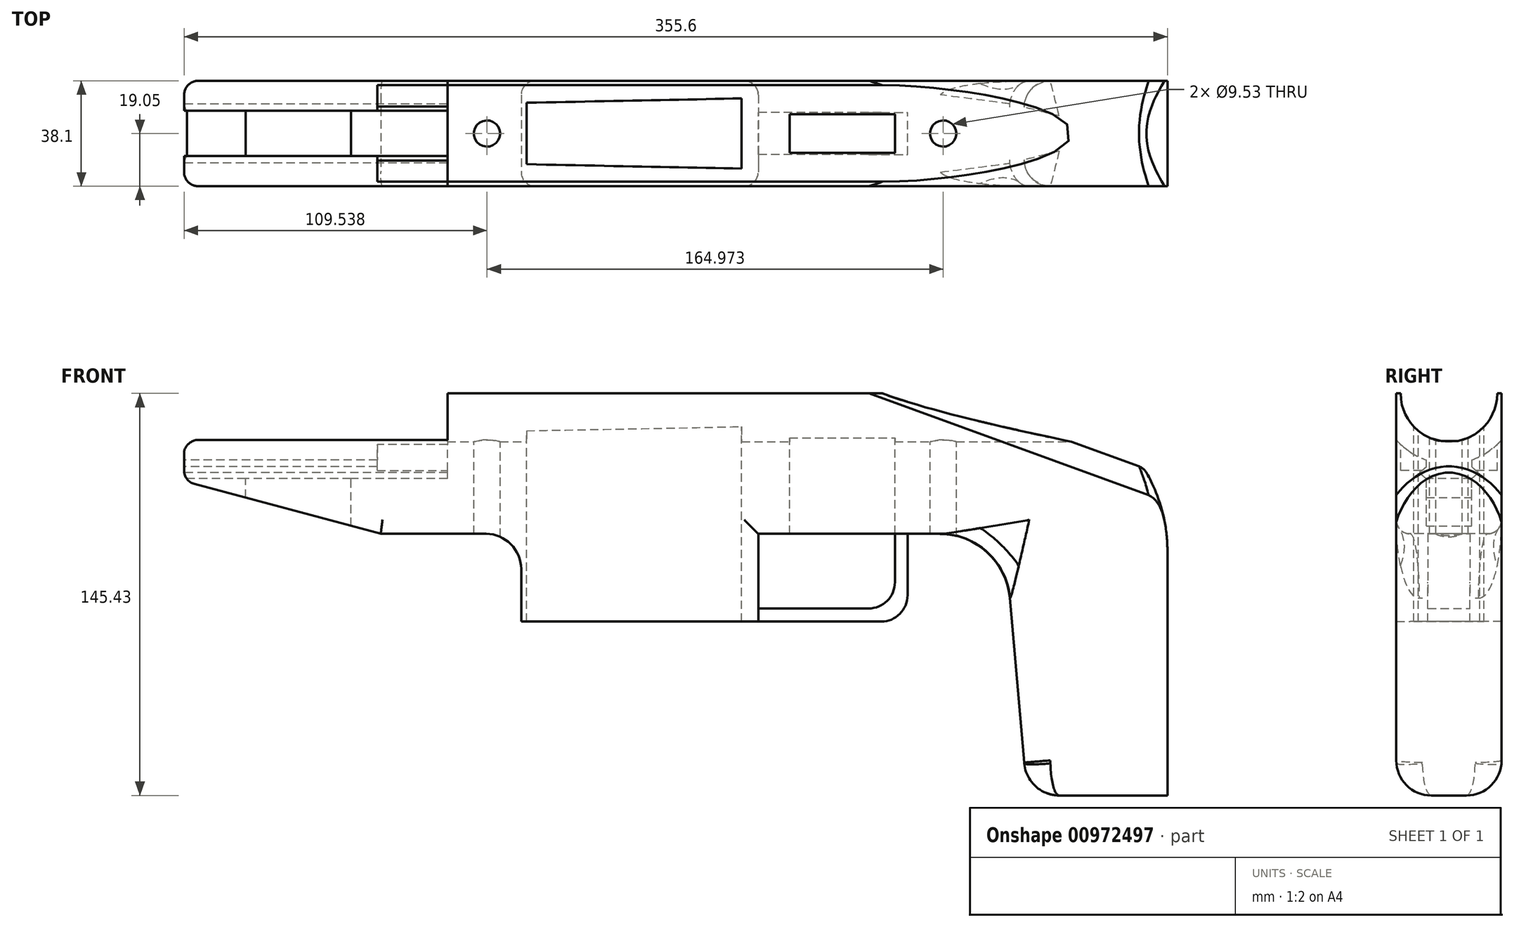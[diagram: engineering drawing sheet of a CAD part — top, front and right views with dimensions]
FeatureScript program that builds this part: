
annotation { "Feature Type Name" : "Feature", "Feature Type Description" : "" }
export const myFeature = defineFeature(function(context is Context, id is Id, definition is map)
    precondition{}
    {
        {
            var Q0;
            Q0=qCreatedBy(makeId("Front.planeOp"),FACE);
            var sketch = newSketch(context, id + "F0", { "sketchPlane" : qUnion([Q0])});
            skLineSegment(sketch, "E0", {"start": v(177.8, -57.15) * mm, "end": v(177.8, -145.43) * mm});
            skLineSegment(sketch, "E1", {"start": v(177.8, -145.43) * mm, "end": v(127, -145.43) * mm});
            skLineSegment(sketch, "E2", {"start": v(127, -145.43) * mm, "end": v(118.72, -50.8) * mm});
            skLineSegment(sketch, "E3", {"start": v(118.72, -50.8) * mm, "end": v(29.82, -50.8) * mm});
            skLineSegment(sketch, "E4", {"start": v(29.82, -50.8) * mm, "end": v(29.82, -82.55) * mm});
            skLineSegment(sketch, "E5", {"start": v(29.82, -82.55) * mm, "end": v(-55.9, -82.55) * mm});
            skLineSegment(sketch, "E6", {"start": v(-55.9, -82.55) * mm, "end": v(-55.9, -50.8) * mm});
            skLineSegment(sketch, "E7", {"start": v(-55.9, -50.8) * mm, "end": v(-106.7, -50.8) * mm});
            skLineSegment(sketch, "E8", {"start": v(-106.7, -50.8) * mm, "end": v(-177.8, -31.75) * mm});
            skLineSegment(sketch, "E9", {"start": v(-177.8, -31.75) * mm, "end": v(-177.8, -9.53) * mm});
            skLineSegment(sketch, "E10", {"start": v(-107.95, -9.53) * mm, "end": v(-107.95, 0) * mm});
            skLineSegment(sketch, "E11", {"start": v(-107.95, 0) * mm, "end": v(120.65, 0) * mm});
            skLineSegment(sketch, "E12", {"start": v(-107.95, -9.53) * mm, "end": v(-177.8, -9.53) * mm});
            skArc(sketch, "E13", {"start": v(177.8, -57.15) * mm, "mid": v(161.06, -16.74) * mm, "end": v(120.65, 0) * mm});
            skLineSegment(sketch, "E14", {"start": v(0, 57.34) * mm, "end": v(0, -146.77) * mm, "construction": true});
            skSolve(sketch);
        }
        {
            var Q0;
            Q0=makeQuery(id+"F0.imprint","IMPRINT",FACE,{"disambiguationData":[TD([[makeQuery(id+"F0.imprint","IMPRINT",EDGE,{"derivedFrom":sQuery(id+"F0.wireOp",EDGE,"E0")}),-1.0]])]});
            extrude(context, id + "F1", {"entities" : qUnion([Q0]), "oppositeDirection" : true, "depth" : 19.05 * mm, "offsetDistance" : 25.4 * mm, "hasSecondDirection" : true, "secondDirectionOppositeDirection" : false, "secondDirectionDepth" : 19.05 * mm});
        }
        {
            var Q0;
            Q0=makeQuery(id+"F1.opExtrude","CAP_EDGE",EDGE,{"disambiguationData":[OSD([sQuery(id+"F0.wireOp",EDGE,"E2")])],"isStart":true});
            var Q1;
            Q1=makeQuery(id+"F1.opExtrude","CAP_EDGE",EDGE,{"disambiguationData":[OSD([sQuery(id+"F0.wireOp",EDGE,"E2")])],"isStart":false});
            fillet(context, id + "F2", {"entities" : qUnion([Q0, Q1]), "radius" : 9.52 * mm, "tangentPropagation" : true, "allowEdgeOverflow" : false});
        }
        {
            var Q0;
            Q0=makeQuery(id+"F1.opExtrude","CAP_EDGE",EDGE,{"disambiguationData":[OSD([sQuery(id+"F0.wireOp",EDGE,"E1")])],"isStart":false});
            fillet(context, id + "F3", {"entities" : qUnion([Q0]), "radius" : 12.7 * mm, "tangentPropagation" : true, "allowEdgeOverflow" : false});
        }
        {
            var Q0;
            Q0=makeQuery(id+"F1.opExtrude","SWEPT_EDGE",EDGE,{"disambiguationData":[OSD([sQuery(id+"F0.wireOp",EDGE,"E6"),sQuery(id+"F0.wireOp",EDGE,"E7")])]});
            fillet(context, id + "F4", {"entities" : qUnion([Q0]), "radius" : 12.7 * mm, "tangentPropagation" : true, "allowEdgeOverflow" : false});
        }
        {
            var Q0;
            Q0=makeQuery(id+"F1.opExtrude","CAP_EDGE",EDGE,{"disambiguationData":[OSD([sQuery(id+"F0.wireOp",EDGE,"E3")])],"isStart":true});
            var Q1;
            Q1=makeQuery(id+"F1.opExtrude","CAP_EDGE",EDGE,{"disambiguationData":[OSD([sQuery(id+"F0.wireOp",EDGE,"E4")])],"isStart":true});
            var Q2;
            Q2=makeQuery(id+"F1.opExtrude","CAP_EDGE",EDGE,{"disambiguationData":[OSD([sQuery(id+"F0.wireOp",EDGE,"E6")])],"isStart":true});
            var Q3;
            Q3=makeQuery(id+"F1.opExtrude","CAP_EDGE",EDGE,{"disambiguationData":[OSD([sQuery(id+"F0.wireOp",EDGE,"E8")])],"isStart":true});
            var Q4;
            Q4=makeQuery(id+"F1.opExtrude","CAP_EDGE",EDGE,{"disambiguationData":[OSD([sQuery(id+"F0.wireOp",EDGE,"E3")])],"isStart":false});
            var Q5;
            Q5=makeQuery(id+"F1.opExtrude","CAP_EDGE",EDGE,{"disambiguationData":[OSD([sQuery(id+"F0.wireOp",EDGE,"E6")])],"isStart":false});
            var Q6;
            Q6=makeQuery(id+"F1.opExtrude","CAP_EDGE",EDGE,{"disambiguationData":[OSD([sQuery(id+"F0.wireOp",EDGE,"E8")])],"isStart":false});
            var Q7;
            Q7=makeQuery(id+"F1.opExtrude","CAP_EDGE",EDGE,{"disambiguationData":[OSD([sQuery(id+"F0.wireOp",EDGE,"E4")])],"isStart":false});
            fillet(context, id + "F5", {"entities" : qUnion([Q0, Q1, Q2, Q3, Q4, Q5, Q6, Q7]), "radius" : 5.08 * mm, "tangentPropagation" : true, "allowEdgeOverflow" : false});
        }
        {
            var Q0;
            Q0=makeQuery(id+"F1.opExtrude","CAP_EDGE",EDGE,{"disambiguationData":[OSD([sQuery(id+"F0.wireOp",EDGE,"E9")])],"isStart":false});
            fillet(context, id + "F6", {"entities" : qUnion([Q0]), "radius" : 5.08 * mm, "tangentPropagation" : true, "allowEdgeOverflow" : false});
        }
        {
            var Q0;
            Q0=qCreatedBy(makeId("Right.planeOp"),FACE);
            var sketch = newSketch(context, id + "F7", { "sketchPlane" : qUnion([Q0])});
            skCircle(sketch, "E15", {"center": v(0, 0) * mm, "radius": 17.46 * mm});
            skSolve(sketch);
        }
        {
            var Q0;
            Q0=makeQuery(id+"F7.imprint","IMPRINT",FACE,{"disambiguationData":[TD([[makeQuery(id+"F7.imprint","IMPRINT",EDGE,{"derivedFrom":sQuery(id+"F7.wireOp",EDGE,"E15")}),1.0]])]});
            extrude(context, id + "F8", {"entities" : qUnion([Q0]), "operationType" : NewBodyOperationType.REMOVE, "endBound" : BoundingType.THROUGH_ALL, "oppositeDirection" : true, "depth" : 25.4 * mm, "offsetDistance" : 25.4 * mm, "hasSecondDirection" : true, "secondDirectionBound" : SecondDirectionBoundingType.THROUGH_ALL, "secondDirectionOppositeDirection" : false, "secondDirectionDepth" : 25.4 * mm});
        }
        {
            var Q0;
            Q0=makeQuery(id+"F1.opExtrude","SWEPT_FACE",FACE,{"disambiguationData":[OSD([sQuery(id+"F0.wireOp",EDGE,"E9")])]});
            var sketch = newSketch(context, id + "F9", { "sketchPlane" : qUnion([Q0])});
            skLineSegment(sketch, "E16", {"start": v(0, 0) * mm, "end": v(0, -58.85) * mm, "construction": true});
            skPoint(sketch, "E16.endSnap0", {"position": v(0, -27.85) * mm});
            skLineSegment(sketch, "E17", {"start": v(-8.2, -24.04) * mm, "end": v(-8.2, -26.54) * mm});
            skLineSegment(sketch, "E18", {"start": v(-8.2, -26.54) * mm, "end": v(-10.67, -28.7) * mm});
            skLineSegment(sketch, "E19", {"start": v(-10.67, -28.7) * mm, "end": v(-8.2, -30.86) * mm});
            skLineSegment(sketch, "E20", {"start": v(-8.2, -30.86) * mm, "end": v(8.2, -30.86) * mm});
            skLineSegment(sketch, "E21", {"start": v(8.2, -30.86) * mm, "end": v(10.67, -28.7) * mm});
            skLineSegment(sketch, "E22", {"start": v(10.67, -28.7) * mm, "end": v(8.2, -26.54) * mm});
            skLineSegment(sketch, "E23", {"start": v(8.2, -26.54) * mm, "end": v(8.2, -24.04) * mm});
            skLineSegment(sketch, "E24", {"start": v(-10.67, -28.7) * mm, "end": v(10.67, -28.7) * mm, "construction": true});
            skArc(sketch, "E25", {"start": v(8.2, -24.04) * mm, "mid": v(0, 25.4) * mm, "end": v(-8.2, -24.04) * mm});
            skPoint(sketch, "E26.orphan", {"position": v(-8.2, -10.48) * mm});
            skPoint(sketch, "E27.orphan", {"position": v(8.2, -10.48) * mm});
            skSolve(sketch);
        }
        {
            var Q0;
            {var subQ11=sQuery(id+"F9.wireOp",EDGE,"E17");Q0=makeQuery(id+"F9.imprint","IMPRINT",FACE,{"disambiguationData":[TD([[makeQuery(id+"F9.imprint","IMPRINT",EDGE,{"derivedFrom":subQ11}),1.0]])]});}
            var Q1;
            {var subQ1=sQuery(id+"F0.wireOp",EDGE,"E9");var subQ2=makeQuery(id+"F1.opExtrude","SWEPT_FACE",FACE,{"disambiguationData":[OSD([subQ1])]});var subQ7=makeQuery(id+"F8.boolean.opBoolean","INTERSECT",EDGE,{"derivedFrom":[subQ2,makeQuery(id+"F8.opExtrude","SWEPT_FACE",FACE,{"disambiguationData":[OSD([sQuery(id+"F7.wireOp",EDGE,"E15")])]})]});Q1=makeQuery(id+"F9.imprint","IMPRINT",FACE,{"disambiguationData":[TD([[makeQuery(id+"F9.imprint","IMPRINT",EDGE,{"derivedFrom":subQ7}),-1.0]])]});}
            var Q2;
            {var subQ0=sQuery(id+"F0.wireOp",EDGE,"E12");var subQ1=sQuery(id+"F0.wireOp",EDGE,"E11");var subQ2=sQuery(id+"F0.wireOp",EDGE,"E10");Q2=makeQuery(id+"F8.boolean.opBoolean","SPLIT",FACE,{"disambiguationData":[TD([makeQuery(id+"F1.opExtrude","CAP_FACE",FACE,{"disambiguationData":[OSD([sQuery(id+"F0.wireOp",EDGE,"E0"),sQuery(id+"F0.wireOp",EDGE,"E1"),sQuery(id+"F0.wireOp",EDGE,"E2"),sQuery(id+"F0.wireOp",EDGE,"E3"),sQuery(id+"F0.wireOp",EDGE,"E4"),sQuery(id+"F0.wireOp",EDGE,"E5"),sQuery(id+"F0.wireOp",EDGE,"E6"),sQuery(id+"F0.wireOp",EDGE,"E7"),sQuery(id+"F0.wireOp",EDGE,"E8"),sQuery(id+"F0.wireOp",EDGE,"E9"),subQ2,subQ1,subQ0,sQuery(id+"F0.wireOp",EDGE,"E13")])],"isStart":true})])],"derivedFrom":makeQuery(id+"F1.opExtrude","SWEPT_FACE",FACE,{"disambiguationData":[OSD([subQ2])]})});}
            extrude(context, id + "F10", {"entities" : qUnion([Q0, Q1]), "operationType" : NewBodyOperationType.REMOVE, "endBound" : BoundingType.UP_TO_SURFACE, "oppositeDirection" : true, "depth" : 25.4 * mm, "endBoundEntityFace" : qUnion([Q2]), "offsetDistance" : 25.4 * mm});
        }
        {
            var Q0;
            Q0=qCreatedBy(makeId("Top.planeOp"),FACE);
            var sketch = newSketch(context, id + "F11", { "sketchPlane" : qUnion([Q0])});
            skPoint(sketch, "E28.0", {"position": v(-107.95, 0) * mm});
            skLineSegment(sketch, "E29", {"start": v(-107.95, 0) * mm, "end": v(-78.77, 0) * mm, "construction": true});
            skCircle(sketch, "E30", {"center": v(-68.26, 0) * mm, "radius": 4.76 * mm});
            skCircle(sketch, "E31", {"center": v(96.71, 0) * mm, "radius": 4.76 * mm});
            skSolve(sketch);
        }
        {
            var Q0;
            Q0 = qSketchRegion(id + "F11", true);
            extrude(context, id + "F12", {"entities" : qUnion([Q0]), "operationType" : NewBodyOperationType.REMOVE, "endBound" : BoundingType.THROUGH_ALL, "oppositeDirection" : true, "depth" : 25.4 * mm, "offsetDistance" : 25.4 * mm});
        }
        {
            var Q0;
            Q0=makeQuery(id+"F1.opExtrude","SWEPT_EDGE",EDGE,{"disambiguationData":[OSD([sQuery(id+"F0.wireOp",EDGE,"E0"),sQuery(id+"F0.wireOp",EDGE,"E13")])]});
            cPlane(context, id + "F13", {"entities" : qUnion([Q0]), "cplaneType" : CPlaneType.LINE_ANGLE, "offset" : 25.4 * mm, "angle" : 110 * degree, "oppositeDirection" : true, "width" : 152.4 * mm, "height" : 152.4 * mm});
        }
        {
            var Q0;
            Q0=qCreatedBy(id+"F13.planeOp",FACE);
            var sketch = newSketch(context, id + "F14", { "sketchPlane" : qUnion([Q0])});
            skArc(sketch, "E32", {"start": v(19.05, 23.9) * mm, "mid": v(0, 32.5) * mm, "end": v(-19.05, 23.9) * mm});
            skLineSegment(sketch, "E33.0", {"start": v(19.05, 23.9) * mm, "end": v(19.05, 44.71) * mm});
            skLineSegment(sketch, "E34.0", {"start": v(-19.05, 23.9) * mm, "end": v(-19.05, 44.71) * mm});
            skLineSegment(sketch, "E35", {"start": v(19.05, 44.71) * mm, "end": v(-19.05, 44.71) * mm});
            skPoint(sketch, "E36.orphan", {"position": v(-19.05, 7.1) * mm});
            skPoint(sketch, "E37.0.end.orphan", {"position": v(19.05, 7.1) * mm});
            skSolve(sketch);
        }
        {
            var Q0;
            Q0=makeQuery(id+"F14.imprint","IMPRINT",FACE,{"disambiguationData":[TD([[makeQuery(id+"F14.imprint","IMPRINT",EDGE,{"derivedFrom":sQuery(id+"F14.wireOp",EDGE,"E32")}),-1.0]])]});
            extrude(context, id + "F15", {"entities" : qUnion([Q0]), "operationType" : NewBodyOperationType.REMOVE, "endBound" : BoundingType.THROUGH_ALL, "depth" : 25.4 * mm, "offsetDistance" : 25.4 * mm});
        }
        {
            var Q0;
            Q0=makeQuery(id+"F15.boolean.opBoolean","INTERSECT",EDGE,{"derivedFrom":[makeQuery(id+"F1.opExtrude","SWEPT_FACE",FACE,{"disambiguationData":[OSD([sQuery(id+"F0.wireOp",EDGE,"E13")])]}),makeQuery(id+"F15.opExtrude","SWEPT_FACE",FACE,{"disambiguationData":[OSD([sQuery(id+"F14.wireOp",EDGE,"E32")])]})]});
            fillet(context, id + "F16", {"entities" : qUnion([Q0]), "radius" : 5.08 * mm, "tangentPropagation" : true, "allowEdgeOverflow" : false});
        }
        {
            var Q0;
            Q0=qCreatedBy(makeId("Top.planeOp"),FACE);
            var sketch = newSketch(context, id + "F17", { "sketchPlane" : qUnion([Q0])});
            skLineSegment(sketch, "E38.0", {"start": v(-107.95, 17.46) * mm, "end": v(-107.95, -17.46) * mm});
            skLineSegment(sketch, "E39.0", {"start": v(-107.95, 17.46) * mm, "end": v(-82.55, 17.46) * mm});
            skLineSegment(sketch, "E40.0", {"start": v(-82.55, -17.46) * mm, "end": v(-107.95, -17.46) * mm});
            skLineSegment(sketch, "E41", {"start": v(-82.55, 17.46) * mm, "end": v(-82.55, -17.46) * mm});
            skPoint(sketch, "E42.orphan", {"position": v(74.71, 17.46) * mm});
            skPoint(sketch, "E43.orphan", {"position": v(74.71, -17.46) * mm});
            skSolve(sketch);
        }
        {
            var Q0;
            Q0=makeQuery(id+"F17.imprint","IMPRINT",FACE,{"disambiguationData":[TD([[makeQuery(id+"F17.imprint","IMPRINT",EDGE,{"derivedFrom":sQuery(id+"F17.wireOp",EDGE,"E38.0")}),1.0]])]});
            extrude(context, id + "F18", {"entities" : qUnion([Q0]), "operationType" : NewBodyOperationType.REMOVE, "oppositeDirection" : true, "depth" : 27.94 * mm, "offsetDistance" : 25.4 * mm});
        }
        {
            var Q0;
            Q0=qCreatedBy(makeId("Top.planeOp"),FACE);
            var sketch = newSketch(context, id + "F19", { "sketchPlane" : qUnion([Q0])});
            skLineSegment(sketch, "E44.0", {"start": v(-177.8, 9.7) * mm, "end": v(-177.8, -9.7) * mm, "construction": true});
            skLineSegment(sketch, "E45.0", {"start": v(-107.95, 9.7) * mm, "end": v(-107.95, -9.7) * mm, "construction": true});
            skLineSegment(sketch, "E46.0", {"start": v(-107.95, 8.2) * mm, "end": v(-177.8, 8.2) * mm});
            skLineSegment(sketch, "E47.0", {"start": v(-107.95, -8.2) * mm, "end": v(-177.8, -8.2) * mm});
            skLineSegment(sketch, "E48", {"start": v(-117.48, -8.2) * mm, "end": v(-117.48, 8.2) * mm});
            skLineSegment(sketch, "E49", {"start": v(-155.58, -8.2) * mm, "end": v(-155.58, 8.2) * mm});
            skSolve(sketch);
        }
        {
            var Q0;
            {var subQ0=sQuery(id+"F19.wireOp",EDGE,"E48");Q0=makeQuery(id+"F19.imprint","IMPRINT",FACE,{"disambiguationData":[TD([[makeQuery(id+"F19.imprint","IMPRINT",EDGE,{"derivedFrom":subQ0}),1.0]])]});}
            extrude(context, id + "F20", {"entities" : qUnion([Q0]), "operationType" : NewBodyOperationType.REMOVE, "endBound" : BoundingType.THROUGH_ALL, "oppositeDirection" : true, "depth" : 25.4 * mm, "offsetDistance" : 25.4 * mm});
        }
        {
            var Q0;
            Q0=qCreatedBy(makeId("Top.planeOp"),FACE);
            var sketch = newSketch(context, id + "F21", { "sketchPlane" : qUnion([Q0])});
            skLineSegment(sketch, "E50", {"start": v(-76.99, 0) * mm, "end": v(75.98, 0) * mm, "construction": true});
            skLineSegment(sketch, "E51", {"start": v(-53.98, 11.11) * mm, "end": v(-53.98, -11.11) * mm});
            skLineSegment(sketch, "E52", {"start": v(-53.98, -11.11) * mm, "end": v(23.83, -12.7) * mm});
            skLineSegment(sketch, "E53", {"start": v(23.83, -12.7) * mm, "end": v(23.83, 12.7) * mm});
            skLineSegment(sketch, "E54", {"start": v(23.83, 12.7) * mm, "end": v(-53.98, 11.11) * mm});
            skSolve(sketch);
        }
        {
            var Q0;
            Q0=makeQuery(id+"F21.imprint","IMPRINT",FACE,{"disambiguationData":[TD([[makeQuery(id+"F21.imprint","IMPRINT",EDGE,{"derivedFrom":sQuery(id+"F21.wireOp",EDGE,"E51")}),1.0]])]});
            extrude(context, id + "F22", {"entities" : qUnion([Q0]), "operationType" : NewBodyOperationType.REMOVE, "endBound" : BoundingType.THROUGH_ALL, "oppositeDirection" : true, "depth" : 25.4 * mm, "offsetDistance" : 25.4 * mm});
        }
        {
            var Q0;
            Q0 = qSketchRegion(id + "F9", true);
            var Q1;
            Q1=makeQuery(id+"F18.boolean.opBoolean","COPY",FACE,{"derivedFrom":makeQuery(id+"F18.opExtrude","SWEPT_FACE",FACE,{"disambiguationData":[OSD([sQuery(id+"F17.wireOp",EDGE,"E41")])]})});
            extrude(context, id + "F23", {"entities" : qUnion([Q0]), "operationType" : NewBodyOperationType.REMOVE, "endBound" : BoundingType.UP_TO_SURFACE, "oppositeDirection" : true, "depth" : 25.4 * mm, "endBoundEntityFace" : qUnion([Q1]), "offsetDistance" : 25.4 * mm});
        }
        {
            var Q0;
            Q0=qCreatedBy(makeId("Top.planeOp"),FACE);
            var sketch = newSketch(context, id + "F24", { "sketchPlane" : qUnion([Q0])});
            skLineSegment(sketch, "E55", {"start": v(70.26, 0) * mm, "end": v(-50.54, 0) * mm, "construction": true});
            skLineSegment(sketch, "E56", {"start": v(79.25, 6.99) * mm, "end": v(79.25, -6.99) * mm});
            skLineSegment(sketch, "E57", {"start": v(79.25, -6.98) * mm, "end": v(41.15, -6.98) * mm});
            skLineSegment(sketch, "E58", {"start": v(41.15, -6.98) * mm, "end": v(41.15, 6.98) * mm});
            skLineSegment(sketch, "E59", {"start": v(79.25, 6.99) * mm, "end": v(41.15, 6.99) * mm});
            skSolve(sketch);
        }
        {
            var Q0;
            Q0=makeQuery(id+"F24.imprint","IMPRINT",FACE,{"disambiguationData":[TD([[makeQuery(id+"F24.imprint","IMPRINT",EDGE,{"derivedFrom":sQuery(id+"F24.wireOp",EDGE,"E56")}),-1.0]])]});
            var Q1;
            Q1=makeQuery(id+"F1.opExtrude","SWEPT_FACE",FACE,{"disambiguationData":[OSD([sQuery(id+"F0.wireOp",EDGE,"E3")])]});
            extrude(context, id + "F25", {"entities" : qUnion([Q0]), "operationType" : NewBodyOperationType.REMOVE, "endBound" : BoundingType.UP_TO_SURFACE, "oppositeDirection" : true, "depth" : 25.4 * mm, "endBoundEntityFace" : qUnion([Q1]), "offsetDistance" : 25.4 * mm});
        }
        {
            var Q0;
            Q0=qCreatedBy(makeId("Front.planeOp"),FACE);
            var sketch = newSketch(context, id + "F26", { "sketchPlane" : qUnion([Q0])});
            skLineSegment(sketch, "E60.0", {"start": v(29.82, -50.8) * mm, "end": v(119.83, -50.8) * mm});
            skLineSegment(sketch, "E61.0", {"start": v(29.82, -82.55) * mm, "end": v(29.82, -50.8) * mm});
            skLineSegment(sketch, "E62", {"start": v(83.8, -50.8) * mm, "end": v(83.8, -82.55) * mm});
            skLineSegment(sketch, "E63", {"start": v(83.8, -82.55) * mm, "end": v(29.82, -82.55) * mm});
            skPoint(sketch, "E64.0", {"position": v(79.25, -50.8) * mm});
            skLineSegment(sketch, "E65", {"start": v(79.25, -50.8) * mm, "end": v(79.25, -77.79) * mm});
            skLineSegment(sketch, "E66", {"start": v(79.25, -77.79) * mm, "end": v(29.82, -77.79) * mm});
            skSolve(sketch);
        }
        {
            var Q0;
            {var subQ1=sQuery(id+"F26.wireOp",EDGE,"E62");Q0=makeQuery(id+"F26.imprint","IMPRINT",FACE,{"disambiguationData":[TD([[makeQuery(id+"F26.imprint","IMPRINT",EDGE,{"derivedFrom":subQ1}),-1.0]])]});}
            extrude(context, id + "F27", {"entities" : qUnion([Q0]), "operationType" : NewBodyOperationType.ADD, "depth" : 7.62 * mm, "offsetDistance" : 25.4 * mm, "hasSecondDirection" : true, "secondDirectionOppositeDirection" : true, "secondDirectionDepth" : 7.62 * mm});
        }
        {
            var Q0;
            Q0=makeQuery(id+"F27.opExtrude","SWEPT_EDGE",EDGE,{"disambiguationData":[OSD([sQuery(id+"F26.wireOp",EDGE,"E62"),sQuery(id+"F26.wireOp",EDGE,"E63")])]});
            var Q1;
            Q1=makeQuery(id+"F27.opExtrude","SWEPT_EDGE",EDGE,{"disambiguationData":[OSD([sQuery(id+"F26.wireOp",EDGE,"E60.0"),sQuery(id+"F26.wireOp",EDGE,"E62")])]});
            var Q2;
            Q2=makeQuery(id+"F27.opExtrude","SWEPT_EDGE",EDGE,{"disambiguationData":[OSD([sQuery(id+"F26.wireOp",EDGE,"E65"),sQuery(id+"F26.wireOp",EDGE,"E66")])]});
            var Q3;
            Q3=makeQuery(id+"F27.opExtrude","SWEPT_EDGE",EDGE,{"disambiguationData":[OSD([sQuery(id+"F26.wireOp",EDGE,"E61.0"),sQuery(id+"F26.wireOp",EDGE,"E66")])]});
            fillet(context, id + "F28", {"entities" : qUnion([Q0, Q1, Q2, Q3]), "radius" : 9.52 * mm, "tangentPropagation" : true, "allowEdgeOverflow" : false});
        }
        {
            var Q0;
            Q0=makeQuery(id+"F1.opExtrude","SWEPT_EDGE",EDGE,{"disambiguationData":[OSD([sQuery(id+"F0.wireOp",EDGE,"E2"),sQuery(id+"F0.wireOp",EDGE,"E3")])]});
            fillet(context, id + "F29", {"entities" : qUnion([Q0]), "radius" : 25.4 * mm, "tangentPropagation" : true, "allowEdgeOverflow" : false});
        }
    });
